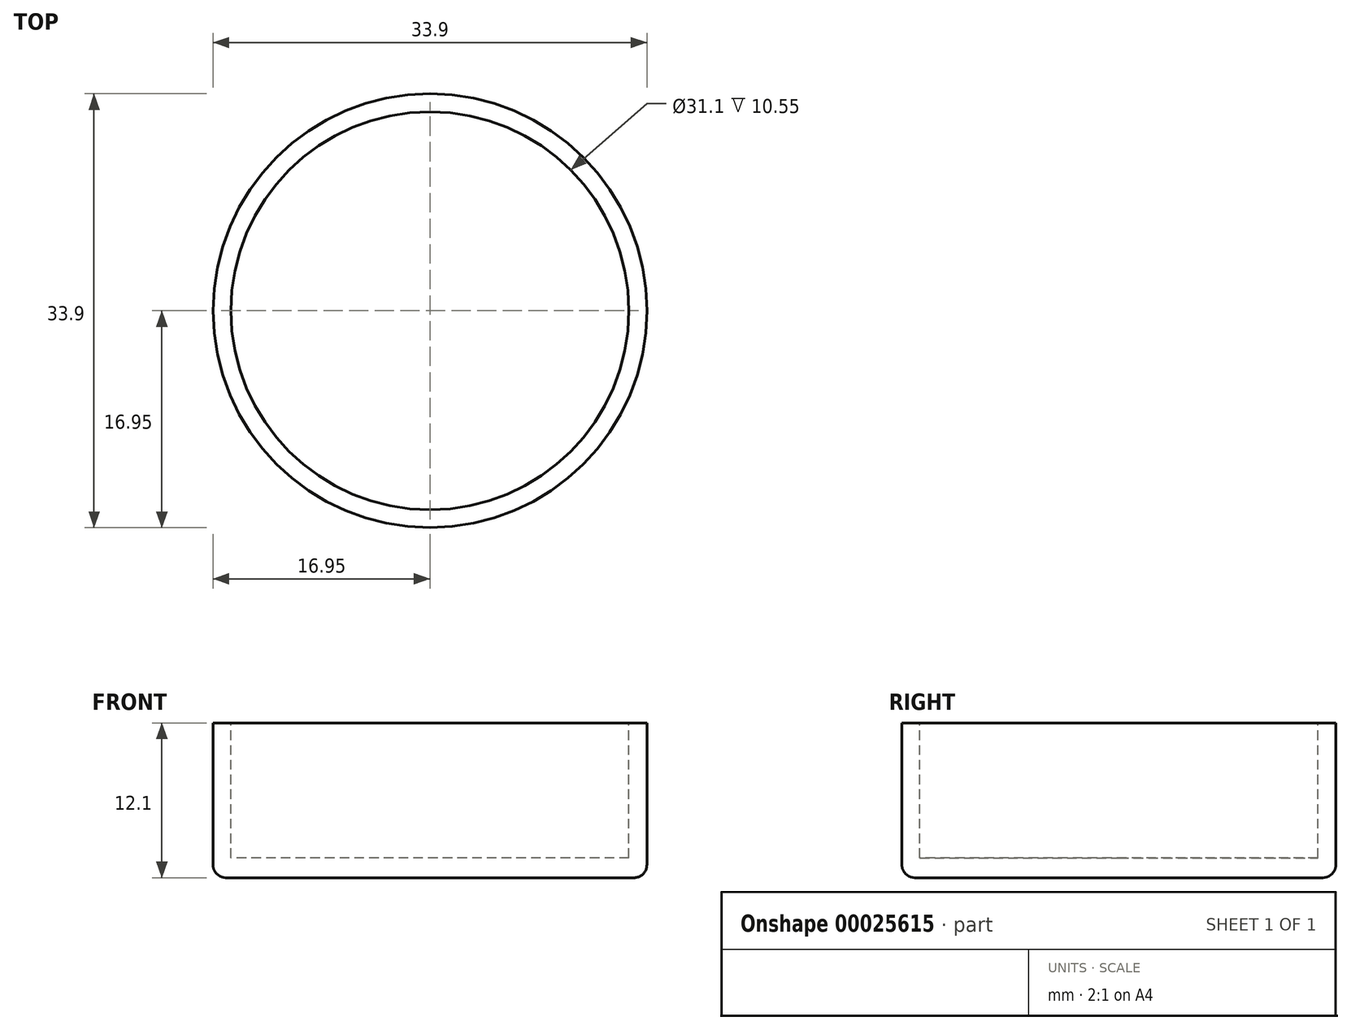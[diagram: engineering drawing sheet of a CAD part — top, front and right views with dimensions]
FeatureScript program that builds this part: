
annotation { "Feature Type Name" : "Feature", "Feature Type Description" : "" }
export const myFeature = defineFeature(function(context is Context, id is Id, definition is map)
    precondition{}
    {
        {
            var Q0;
            Q0=qCreatedBy(makeId("Top.planeOp"),FACE);
            var sketch = newSketch(context, id + "F0", { "sketchPlane" : qUnion([Q0])});
            skCircle(sketch, "E0", {"center": v(0, 0) * mm, "radius": 16.95 * mm});
            skSolve(sketch);
        }
        {
            var Q0;
            Q0 = qSketchRegion(id + "F0", true);
            extrude(context, id + "F1", {"entities" : qUnion([Q0]), "depth" : 12.1 * mm});
        }
        {
            var Q0;
            Q0=makeQuery(id+"F1.opExtrude","CAP_FACE",FACE,{"disambiguationData":[OSD([sQuery(id+"F0.wireOp",EDGE,"E0")])],"isStart":false});
            var sketch = newSketch(context, id + "F2", { "sketchPlane" : qUnion([Q0])});
            skCircle(sketch, "E1", {"center": v(0, 0) * mm, "radius": 15.55 * mm});
            skSolve(sketch);
        }
        {
            var Q0;
            Q0 = qSketchRegion(id + "F2", true);
            extrude(context, id + "F3", {"entities" : qUnion([Q0]), "operationType" : NewBodyOperationType.REMOVE, "oppositeDirection" : true, "depth" : 10.55 * mm});
        }
        {
            var Q0;
            Q0=makeQuery(id+"F1.opExtrude","CAP_EDGE",EDGE,{"disambiguationData":[OSD([sQuery(id+"F0.wireOp",EDGE,"E0")])],"isStart":true});
            fillet(context, id + "F4", {"entities" : qUnion([Q0]), "radius" : 1 * mm, "tangentPropagation" : true, "allowEdgeOverflow" : false});
        }
    });
